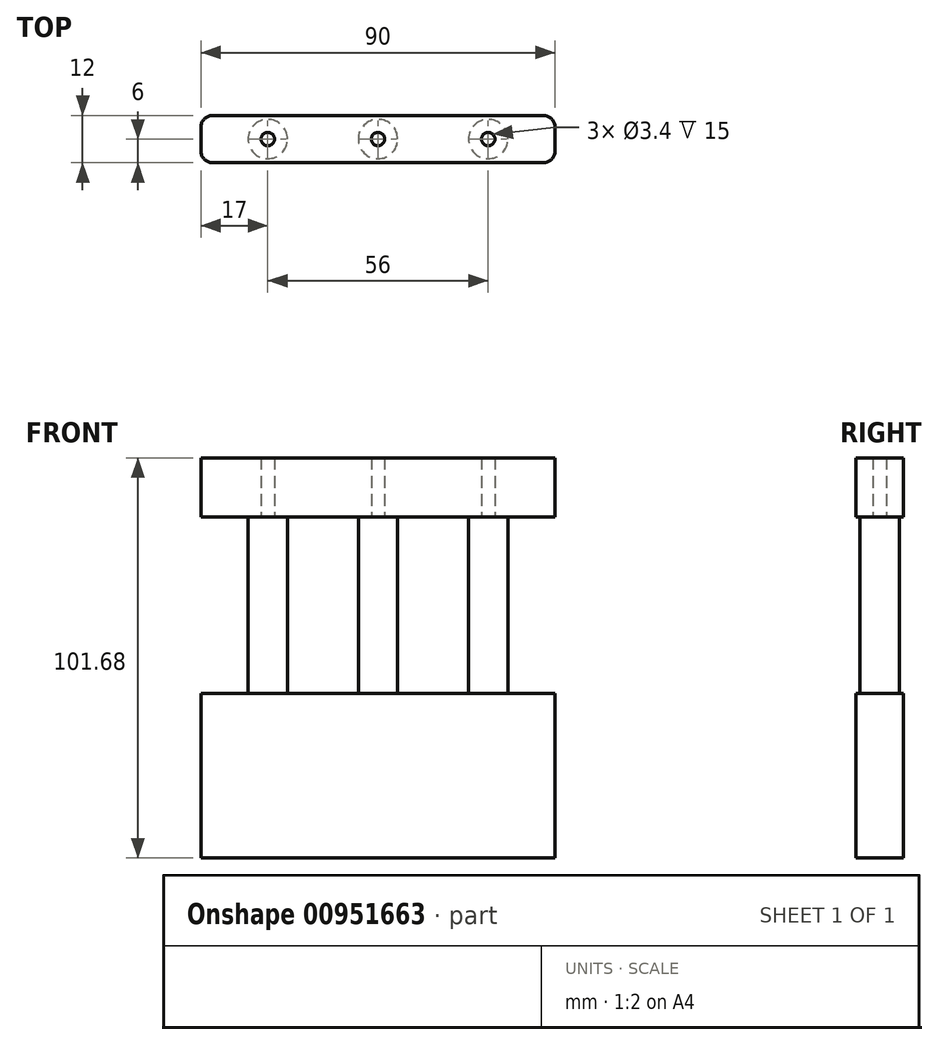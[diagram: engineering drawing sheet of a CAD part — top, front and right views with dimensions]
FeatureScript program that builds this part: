
annotation { "Feature Type Name" : "Feature", "Feature Type Description" : "" }
export const myFeature = defineFeature(function(context is Context, id is Id, definition is map)
    precondition{}
    {
        {
            var Q0;
            Q0=qCreatedBy(makeId("Front.planeOp"),FACE);
            var sketch = newSketch(context, id + "F0", { "sketchPlane" : qUnion([Q0])});
            skLineSegment(sketch, "E0.bottom", {"start": v(-45, 20.89) * mm, "end": v(45, 20.89) * mm});
            skLineSegment(sketch, "E0.top", {"start": v(-45, -20.89) * mm, "end": v(45, -20.89) * mm});
            skLineSegment(sketch, "E0.left", {"start": v(-45, 20.89) * mm, "end": v(-45, -20.89) * mm});
            skLineSegment(sketch, "E0.right", {"start": v(45, 20.89) * mm, "end": v(45, -20.89) * mm});
            skPoint(sketch, "E0.middle", {"position": v(0, 0) * mm});
            skSolve(sketch);
        }
        {
            var Q0;
            Q0=makeQuery(id+"F0.imprint","IMPRINT",FACE,{"disambiguationData":[TD([[makeQuery(id+"F0.imprint","IMPRINT",EDGE,{"derivedFrom":sQuery(id+"F0.wireOp",EDGE,"E0.bottom")}),-1.0]])]});
            extrude(context, id + "F1", {"entities" : qUnion([Q0]), "endBound" : BoundingType.SYMMETRIC, "depth" : 12 * mm, "offsetDistance" : 25 * mm});
        }
        {
            var Q0;
            Q0=makeQuery(id+"F1.opExtrude","SWEPT_FACE",FACE,{"disambiguationData":[OSD([sQuery(id+"F0.wireOp",EDGE,"E0.bottom")])]});
            var sketch = newSketch(context, id + "F2", { "sketchPlane" : qUnion([Q0])});
            skLineSegment(sketch, "E1", {"start": v(0, 0) * mm, "end": v(28, 0) * mm});
            skLineSegment(sketch, "E2", {"start": v(0, 0) * mm, "end": v(-28, 0) * mm});
            skCircle(sketch, "E3", {"center": v(-28, 0) * mm, "radius": 5 * mm});
            skCircle(sketch, "E4", {"center": v(0, 0) * mm, "radius": 5 * mm});
            skCircle(sketch, "E5", {"center": v(28, 0) * mm, "radius": 5 * mm});
            skLineSegment(sketch, "E6", {"start": v(-28, 0) * mm, "end": v(-45, 0) * mm});
            skSolve(sketch);
        }
        {
            var Q0;
            Q0=makeQuery(id+"F2.imprint","IMPRINT",FACE,{"disambiguationData":[TD([[makeQuery(id+"F2.imprint","IMPRINT",EDGE,{"derivedFrom":sQuery(id+"F2.wireOp",EDGE,"E3")}),1.0]])]});
            var Q1;
            {var subQ0=sQuery(id+"F2.wireOp",EDGE,"E2");var subQ1=sQuery(id+"F2.wireOp",EDGE,"E1");var subQ2=makeQuery(id+"F2.imprint","INTERSECT",VERTEX,{"derivedFrom":[subQ1,subQ0]});Q1=makeQuery(id+"F2.imprint","IMPRINT",FACE,{"disambiguationData":[TD([[makeQuery(id+"F2.imprint","IMPRINT",EDGE,{"disambiguationData":[TD([[subQ2,-1.0]])],"derivedFrom":subQ1}),1.0]])]});}
            var Q2;
            {var subQ0=sQuery(id+"F2.wireOp",EDGE,"E2");var subQ1=sQuery(id+"F2.wireOp",EDGE,"E1");var subQ2=makeQuery(id+"F2.imprint","INTERSECT",VERTEX,{"derivedFrom":[subQ1,subQ0]});Q2=makeQuery(id+"F2.imprint","IMPRINT",FACE,{"disambiguationData":[TD([[makeQuery(id+"F2.imprint","IMPRINT",EDGE,{"disambiguationData":[TD([[subQ2,-1.0]])],"derivedFrom":subQ1}),-1.0]])]});}
            var Q3;
            Q3=makeQuery(id+"F2.imprint","IMPRINT",FACE,{"disambiguationData":[TD([[makeQuery(id+"F2.imprint","IMPRINT",EDGE,{"derivedFrom":sQuery(id+"F2.wireOp",EDGE,"E5")}),1.0]])]});
            extrude(context, id + "F3", {"entities" : qUnion([Q0, Q1, Q2, Q3]), "operationType" : NewBodyOperationType.ADD, "depth" : 44.9 * mm, "offsetDistance" : 25 * mm});
        }
        {
            var Q0;
            Q0=makeQuery(id+"F3.opExtrude","CAP_FACE",FACE,{"disambiguationData":[OSD([sQuery(id+"F2.wireOp",EDGE,"E3")])],"isStart":false});
            var sketch = newSketch(context, id + "F4", { "sketchPlane" : qUnion([Q0])});
            skLineSegment(sketch, "E7.bottom", {"start": v(-45, 6) * mm, "end": v(45, 6) * mm});
            skLineSegment(sketch, "E7.top", {"start": v(-45, -6) * mm, "end": v(45, -6) * mm});
            skLineSegment(sketch, "E7.left", {"start": v(-45, 6) * mm, "end": v(-45, -6) * mm});
            skLineSegment(sketch, "E7.right", {"start": v(45, 6) * mm, "end": v(45, -6) * mm});
            skPoint(sketch, "E7.middle", {"position": v(0, 0) * mm});
            skSolve(sketch);
        }
        {
            var Q0;
            Q0=makeQuery(id+"F4.imprint","IMPRINT",FACE,{"disambiguationData":[TD([[makeQuery(id+"F4.imprint","IMPRINT",EDGE,{"derivedFrom":makeQuery(id+"F3.opExtrude","CAP_EDGE",EDGE,{"disambiguationData":[OSD([sQuery(id+"F2.wireOp",EDGE,"E3")])],"isStart":false})}),1.0]])]});
            var Q1;
            Q1=makeQuery(id+"F4.imprint","IMPRINT",FACE,{"disambiguationData":[TD([[makeQuery(id+"F4.imprint","IMPRINT",EDGE,{"derivedFrom":sQuery(id+"F4.wireOp",EDGE,"E7.bottom")}),-1.0]])]});
            extrude(context, id + "F5", {"entities" : qUnion([Q0, Q1]), "operationType" : NewBodyOperationType.ADD, "depth" : 15 * mm, "offsetDistance" : 25 * mm});
        }
        {
            var Q0;
            Q0=makeQuery(id+"F1.opExtrude","CAP_EDGE",EDGE,{"disambiguationData":[OSD([sQuery(id+"F0.wireOp",EDGE,"E0.right")])],"isStart":false});
            var Q1;
            Q1=makeQuery(id+"F1.opExtrude","CAP_EDGE",EDGE,{"disambiguationData":[OSD([sQuery(id+"F0.wireOp",EDGE,"E0.right")])],"isStart":true});
            var Q2;
            Q2=makeQuery(id+"F1.opExtrude","CAP_EDGE",EDGE,{"disambiguationData":[OSD([sQuery(id+"F0.wireOp",EDGE,"E0.left")])],"isStart":false});
            var Q3;
            Q3=makeQuery(id+"F1.opExtrude","CAP_EDGE",EDGE,{"disambiguationData":[OSD([sQuery(id+"F0.wireOp",EDGE,"E0.left")])],"isStart":true});
            var Q4;
            Q4=makeQuery(id+"F5.opExtrude","SWEPT_EDGE",EDGE,{"disambiguationData":[OSD([sQuery(id+"F4.wireOp",EDGE,"E7.bottom"),sQuery(id+"F4.wireOp",EDGE,"E7.left")])]});
            var Q5;
            Q5=makeQuery(id+"F5.opExtrude","SWEPT_EDGE",EDGE,{"disambiguationData":[OSD([sQuery(id+"F4.wireOp",EDGE,"E7.top"),sQuery(id+"F4.wireOp",EDGE,"E7.left")])]});
            var Q6;
            Q6=makeQuery(id+"F5.opExtrude","SWEPT_EDGE",EDGE,{"disambiguationData":[OSD([sQuery(id+"F4.wireOp",EDGE,"E7.top"),sQuery(id+"F4.wireOp",EDGE,"E7.right")])]});
            var Q7;
            Q7=makeQuery(id+"F5.opExtrude","SWEPT_EDGE",EDGE,{"disambiguationData":[OSD([sQuery(id+"F4.wireOp",EDGE,"E7.bottom"),sQuery(id+"F4.wireOp",EDGE,"E7.right")])]});
            fillet(context, id + "F6", {"entities" : qUnion([Q0, Q1, Q2, Q3, Q4, Q5, Q6, Q7]), "radius" : 3 * mm, "tangentPropagation" : true, "allowEdgeOverflow" : false});
        }
        {
            var Q0;
            Q0=makeQuery(id+"F5.opExtrude","CAP_FACE",FACE,{"disambiguationData":[OSD([sQuery(id+"F4.wireOp",EDGE,"E7.bottom"),sQuery(id+"F4.wireOp",EDGE,"E7.top"),sQuery(id+"F4.wireOp",EDGE,"E7.left"),sQuery(id+"F4.wireOp",EDGE,"E7.right")])],"isStart":true});
            var sketch = newSketch(context, id + "F7", { "sketchPlane" : qUnion([Q0])});
            skCircle(sketch, "E8", {"center": v(-28, 0) * mm, "radius": 1.7 * mm});
            skCircle(sketch, "E9", {"center": v(0, 0) * mm, "radius": 1.7 * mm});
            skCircle(sketch, "E10", {"center": v(28, 0) * mm, "radius": 1.7 * mm});
            skSolve(sketch);
        }
        {
            var Q0;
            Q0 = qSketchRegion(id + "F7", true);
            extrude(context, id + "F8", {"entities" : qUnion([Q0]), "operationType" : NewBodyOperationType.REMOVE, "oppositeDirection" : true, "depth" : 20 * mm, "offsetDistance" : 25 * mm});
        }
    });
